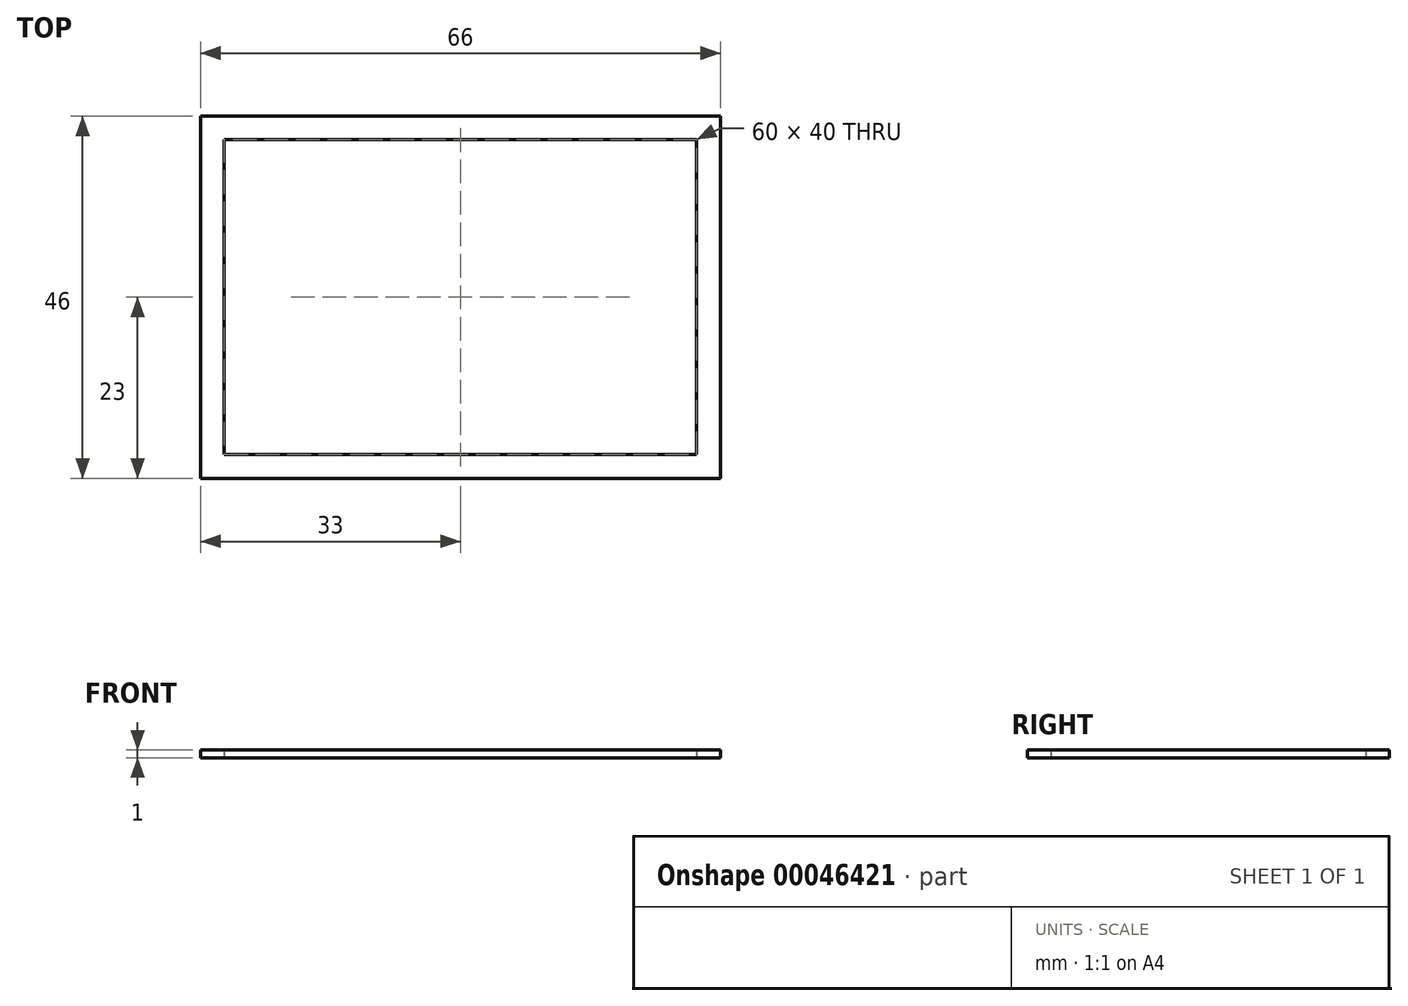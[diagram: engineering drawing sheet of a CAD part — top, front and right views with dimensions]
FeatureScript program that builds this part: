
annotation { "Feature Type Name" : "Feature", "Feature Type Description" : "" }
export const myFeature = defineFeature(function(context is Context, id is Id, definition is map)
    precondition{}
    {
        {
            var Q0;
            Q0=qCreatedBy(makeId("Top.planeOp"),FACE);
            var sketch = newSketch(context, id + "F0", { "sketchPlane" : qUnion([Q0])});
            skLineSegment(sketch, "E0.bottom", {"start": v(30, -20) * mm, "end": v(-30, -20) * mm});
            skLineSegment(sketch, "E0.top", {"start": v(30, 20) * mm, "end": v(-30, 20) * mm});
            skLineSegment(sketch, "E0.left", {"start": v(30, -20) * mm, "end": v(30, 20) * mm});
            skLineSegment(sketch, "E0.right", {"start": v(-30, -20) * mm, "end": v(-30, 20) * mm});
            skPoint(sketch, "E0.middle", {"position": v(0, 0) * mm});
            skLineSegment(sketch, "E1.0", {"start": v(33, -23) * mm, "end": v(-33, -23) * mm});
            skLineSegment(sketch, "E1.1", {"start": v(33, -23) * mm, "end": v(33, 23) * mm});
            skLineSegment(sketch, "E1.2", {"start": v(33, 23) * mm, "end": v(-33, 23) * mm});
            skLineSegment(sketch, "E1.3", {"start": v(-33, -23) * mm, "end": v(-33, 23) * mm});
            skSolve(sketch);
        }
        {
            var Q0;
            Q0=makeQuery(id+"F0.imprint","IMPRINT",FACE,{"disambiguationData":[TD([[makeQuery(id+"F0.imprint","IMPRINT",EDGE,{"derivedFrom":sQuery(id+"F0.wireOp",EDGE,"E0.bottom")}),1.0]])]});
            extrude(context, id + "F1", {"entities" : qUnion([Q0]), "depth" : 1 * mm, "offsetDistance" : 25 * mm});
        }
    });
